FCSTD DOCUMENT  (FreeCAD 0.17R12568 +1 (Git))
Label: lathepart1
License: All rights reserved
LicenseURL: http://en.wikipedia.org/wiki/All_rights_reserved
objects: Sketcher::SketchObject×1, PartDesign::Revolution×1, PartDesign::Body×1
note: 4 computed .brp shape members not serialized (recipe doc carries the construction recipe); baked Part::Feature solids carry a one-line shape summary decoded from their .brp

FEATURE [Sketcher::SketchObject] Sketch
  MapMode = 5
  Placement = pos=(0,0,0) rot=(1,0,0;1.5708rad)
  Support = -> [XZ_Plane]
  sketch-geometry (14):
    g0: LineSegment StartX=0 StartY=0 StartZ=0 EndX=0 EndY=106.809 EndZ=0
    g1: ArcOfCircle CenterX=2e-12 CenterY=90.8094 CenterZ=0 NormalX=0 NormalY=0 NormalZ=1 AngleXU=0 Radius=16 StartAngle=5.26411 EndAngle=7.85398
    g2: LineSegment StartX=16.4298 StartY=68.6957 StartZ=0 EndX=7.92984 EndY=68.6957 EndZ=0
    g3: ArcOfCircle CenterX=60.235 CenterY=70.4555 CenterZ=0 NormalX=0 NormalY=0 NormalZ=1 AngleXU=0 Radius=52.3348 StartAngle=3.17522 EndAngle=3.85901
    g4: ArcOfCircle CenterX=21.5794 CenterY=34.2063 CenterZ=0 NormalX=0 NormalY=0 NormalZ=1 AngleXU=0 Radius=2 StartAngle=4.68047 EndAngle=8.25399
    g5: LineSegment StartX=21.5155 StartY=32.2073 StartZ=0 EndX=21.5155 EndY=30.253 EndZ=0
    g6: LineSegment StartX=21.5155 StartY=30.253 StartZ=0 EndX=23.9729 EndY=30.06 EndZ=0
    g7: ArcOfCircle CenterX=32.9523 CenterY=29.3549 CenterZ=0 NormalX=0 NormalY=0 NormalZ=1 AngleXU=0 Radius=9.00705 StartAngle=3.06323 EndAngle=4.44678
    g8: ArcOfCircle CenterX=29.1528 CenterY=15.3877 CenterZ=0 NormalX=0 NormalY=0 NormalZ=1 AngleXU=0 Radius=5.46781 StartAngle=6.06049 EndAngle=7.58837
    g9: ArcOfCircle CenterX=23.3968 CenterY=16.6911 CenterZ=0 NormalX=0 NormalY=0 NormalZ=1 AngleXU=0 Radius=11.3695 StartAngle=5.50684 EndAngle=6.06049
    g10: LineSegment StartX=31.5087 StartY=8.72476 StartZ=0 EndX=34.7164 EndY=6.47867 EndZ=0
    g11: LineSegment StartX=34.7164 StartY=6.47867 StartZ=0 EndX=36.4524 EndY=0 EndZ=0
    g12: LineSegment StartX=36.4524 StartY=0 StartZ=0 EndX=0 EndY=0 EndZ=0
    g13: ArcOfCircle CenterX=7.92984 CenterY=68.6957 CenterZ=0 NormalX=0 NormalY=0 NormalZ=1 AngleXU=0 Radius=8.5 StartAngle=0 EndAngle=1.51705
  constraints (28):
    c: Coincident(g-1,g0)
    c: PointOnObject(g0,g-2)
    c: Perpendicular(g0,g1) = 1.5708
    c: DistanceY(g0,g0) = 106.809
    c: Coincident(g4,g5)
    c: Coincident(g5,g6)
    c: Perpendicular(g6,g7) = 4.71239
    c: Tangent(g7,g8) = 1.5708
    c: Tangent(g8,g9) = -1.5708
    c: Coincident(g9,g10)
    c: Coincident(g10,g11)
    c: Coincident(g11,g12)
    c: Coincident(g0,g12)
    c: Horizontal(g2)
    c: Radius(g1) = 16
    c: DistanceX(g1) = 8.38644
    c: Coincident(g2,g3)
    c: Coincident(g13,g2)
    c: Coincident(g13,g1)
    c: Coincident(g13,g2)
    c: DistanceX(g2,g2) = 8.5
    c: Vertical(g5)
    c: Coincident(g3,g4)
    c: Radius(g4) = 2
    c: Horizontal(g12)
    c: DistanceX(g12,g12) = 36.4524
    c: Angle(g11,g12) = 1.309
    c: Angle(g10,g11) = 2.44346
FEATURE [PartDesign::Revolution] Revolution  label="Pawn"
  Angle = 360
  Axis = (0,0,1)
  Base = (0,0,0)
  Placement = pos=(0,0,0) rot=(1,0,0;1.5708rad)
  Profile = -> Sketch
  ReferenceAxis = -> Sketch [V_Axis]
  Reversed = true
FEATURE [PartDesign::Body] Body
  Group = -> [Sketch,Revolution]
  Origin = -> BodyOrigin
